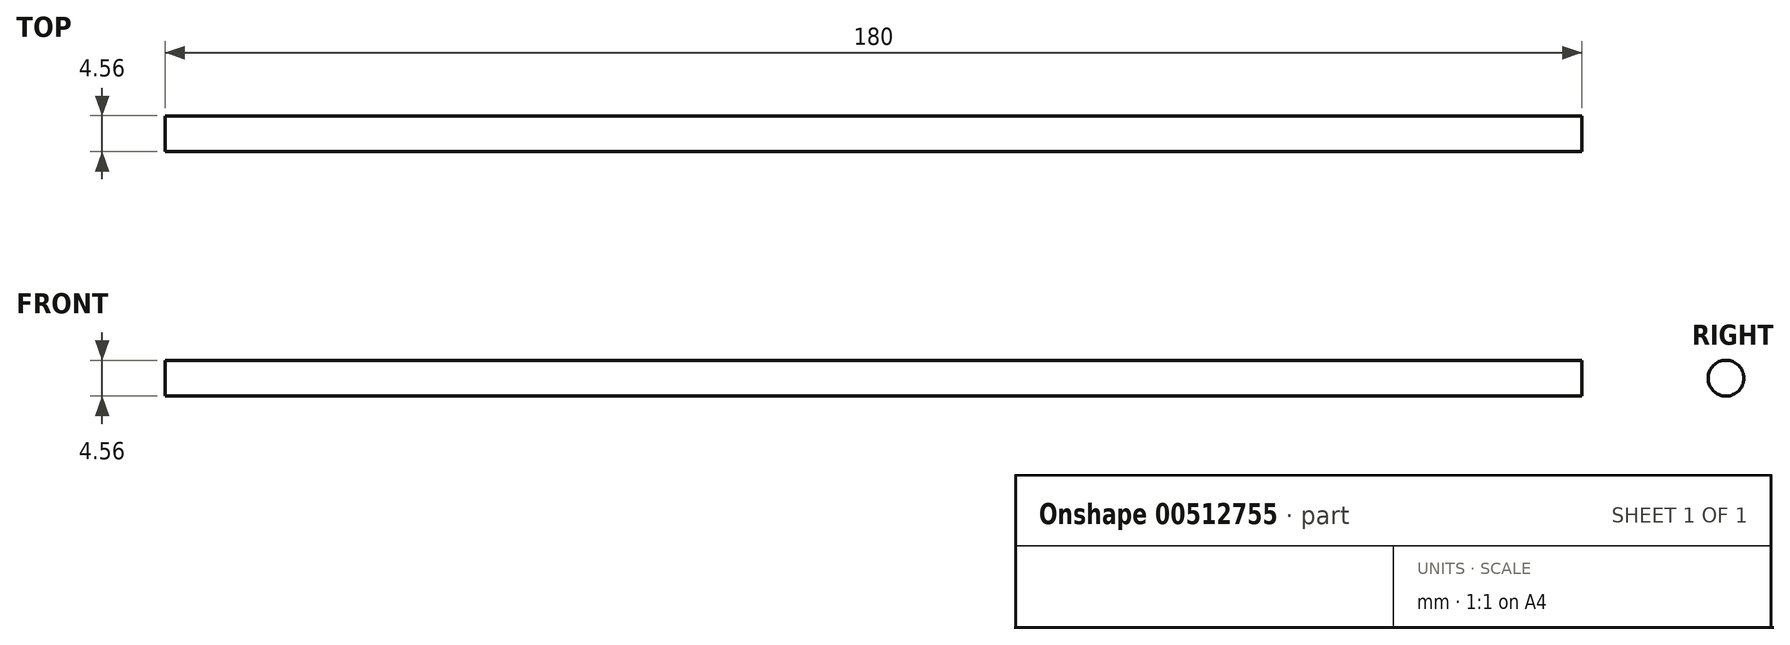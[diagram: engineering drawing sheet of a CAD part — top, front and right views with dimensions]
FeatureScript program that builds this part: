
annotation { "Feature Type Name" : "Feature", "Feature Type Description" : "" }
export const myFeature = defineFeature(function(context is Context, id is Id, definition is map)
    precondition{}
    {
        {
            var Q0;
            Q0=qCreatedBy(makeId("Right.planeOp"),FACE);
            var sketch = newSketch(context, id + "F0", { "sketchPlane" : qUnion([Q0])});
            skCircle(sketch, "E0", {"center": v(0, 0) * mm, "radius": 2.27 * mm});
            skSolve(sketch);
        }
        {
            var Q0;
            Q0 = qSketchRegion(id + "F0", true);
            extrude(context, id + "F1", {"entities" : qUnion([Q0]), "depth" : 180 * mm, "offsetDistance" : 25 * mm});
        }
    });
